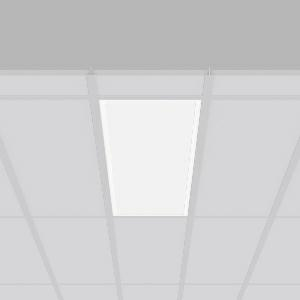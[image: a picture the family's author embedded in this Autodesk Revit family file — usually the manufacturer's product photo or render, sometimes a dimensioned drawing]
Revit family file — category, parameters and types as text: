
# Revit family: sidelite_eco_672372_002_07_b543
name_source: partatom
category: Lighting Fixtures
units: mm (PartAtom-declared; Revit-internal decimal feet)

## family parameters
Cut with Voids When Loaded = No
Host = Face
Light Source = No
Part Type = Normal
Room Calculation Point = No
Round Connector Dimension = Use Diameter
Shared = No

## types (1)
- SIDELITE ECO (1 x LED Modul 830, 3300 lm, 3000)
    Apparent Load = 29 VA
    CIE Flux Codes = 46 79 96 100 100
    Color Rendering = 80
    Color Temperature = 3000
    Default Elevation = 1800 mm
    Description = Series: SIDELITE ECO
Highly economical recessed luminaire with progressive LED technology. For escape route illumination. Frame made of aluminium, powder-coated. Diffuser: plastic, opal. Lightguide and diffuser made of non-yellowing plastic (PMMA). Lateral light emission (RZB SIDELITE technology) for homogeneous light distribution. External driver. Self-contained system with automatic self-test and feedback via DALI bus, only to RZB DALI monitoring system. External driver with simple plug-in locking system. Extended connection cable (1.90 m). 
Colour: white
Length: 1195 mm
Width: 295 mm
Cut-out length: 1170 mm
Cut-out width: 270 mm
Recess height: 160 mm
Luminaire: recess height: 40 mm
Weight: 4.4 kg
Operating mode: maintained power mode
Duration time: 8 h
Lamp: LED
Socket: without socket
Colour temperature: 3000K
Colour rendering index (CRI): 80
System power: 29 W
Rated luminous flux: 3300 lm
Luminous flux, emergency: 220 lm
System power, emergency: -
Control gear: Regulated power supply
Protection class: I
Type of protection: IP 40
    Height = 0 mm  [stored 0 ft]
    Lamp = 1 x LED Modul 830
    Lamp Light Flux = 3300 lm
    Lamp count = 1
    Length = 1195 mm
    Lifetime = 50000 h
    Luminous efficacy = 114 lm/W
    Manufacturer = RZB
    ModVariant = No
    Model = 672372.002.07
    Mounting Place = Ceiling
    Mounting Type = Recessed
    Number of Poles = 1
    OnlyDefault = Yes
    Power Factor = 1
    Product Name = SIDELITE ECO
    Product group = Recessed modular luminaires
    ProductGroupID = 406
    Protection Class = Protection class I
    Protection Degree = IP 40
    RLX_Detail_Level = 1
    RLX_Emergency_Light_Flux = 220 lm
    RLX_Emergency_Type = 3
    RLX_Emergency_Type_DB = Yes
    RlxData = <blob elided: 30701 chars, md5=e4139682>
    Socket = socket
    Standby Power = 0 W
    System Light Flux = 3300 lm
    System Power = 29 W
    Type Comments = Product without accessories
    Type Image = 312365.002.jpg
    URL = http://relux.com
    VarID = ---
    Voltage = 230 V
    Voltage Range = 220-240 V
    Weight = 0.00 kg
    Width = 295 mm

note: [stored X ft] marks values corroborated as IEEE doubles in the binary element streams (Revit-internal decimal feet)

## geometry (parser evidence)
native form markers: Blend x4, Sweep x12
no freeform markers — native parametric forms only
